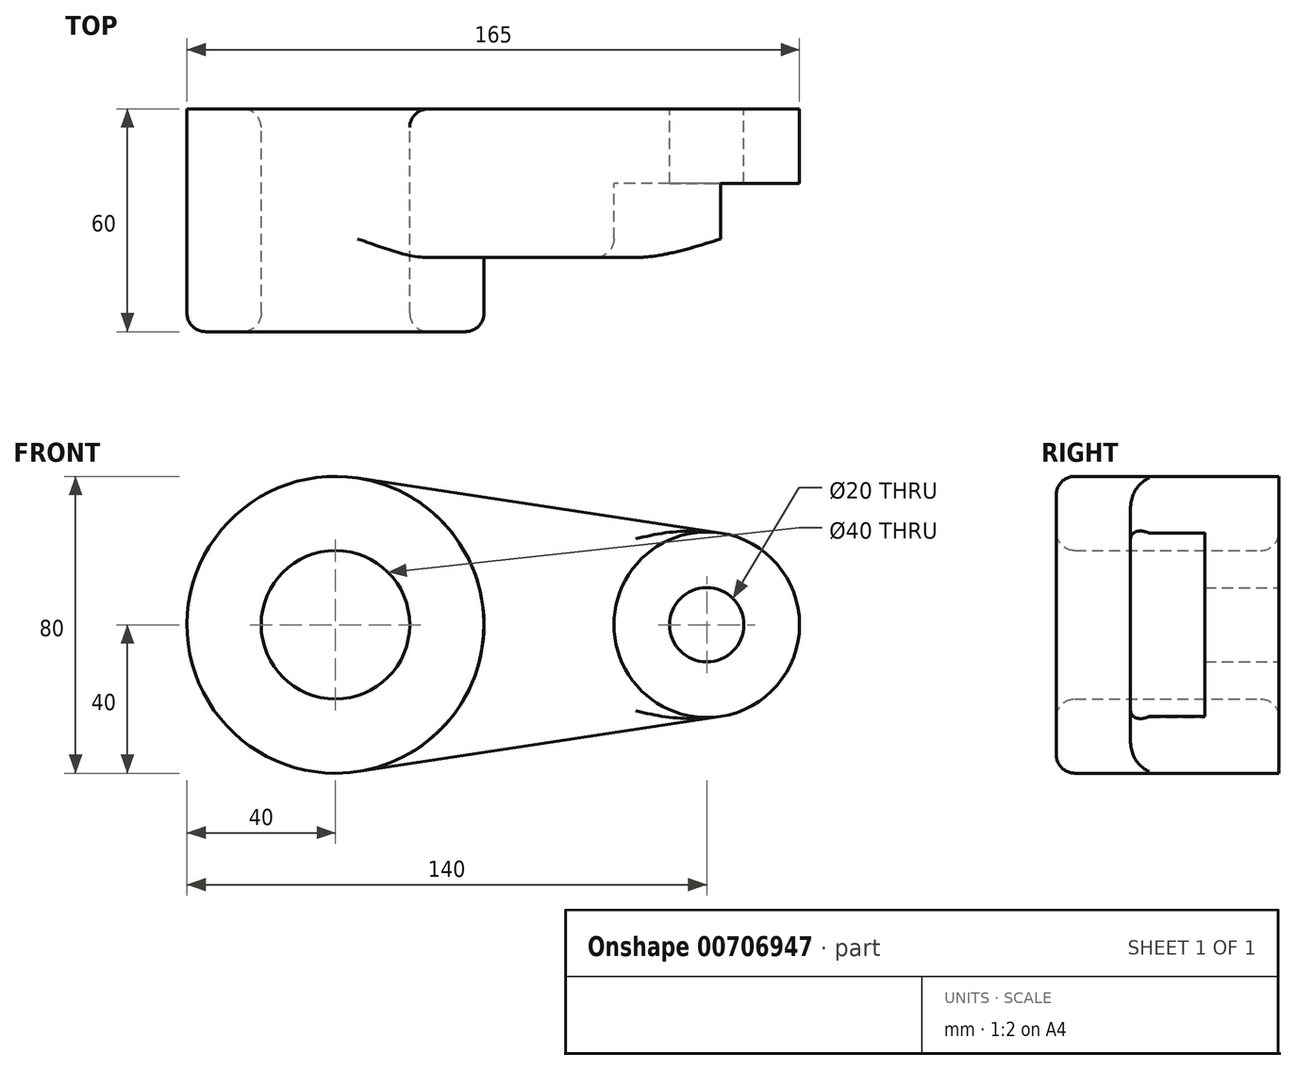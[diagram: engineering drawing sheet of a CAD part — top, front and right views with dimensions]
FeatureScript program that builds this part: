
annotation { "Feature Type Name" : "Feature", "Feature Type Description" : "" }
export const myFeature = defineFeature(function(context is Context, id is Id, definition is map)
    precondition{}
    {
        {
            var Q0;
            Q0=qCreatedBy(makeId("Front.planeOp"),FACE);
            var sketch = newSketch(context, id + "F0", { "sketchPlane" : qUnion([Q0])});
            skCircle(sketch, "E0", {"center": v(-50, 0) * mm, "radius": 40 * mm});
            skCircle(sketch, "E1", {"center": v(-50, 0) * mm, "radius": 20 * mm});
            skCircle(sketch, "E2", {"center": v(50, 0) * mm, "radius": 25 * mm});
            skCircle(sketch, "E3", {"center": v(50, 0) * mm, "radius": 10 * mm});
            skLineSegment(sketch, "E4", {"start": v(-44, 39.55) * mm, "end": v(53.75, 24.72) * mm});
            skLineSegment(sketch, "E5", {"start": v(-44, -39.55) * mm, "end": v(53.75, -24.72) * mm});
            skSolve(sketch);
        }
        {
            var Q0;
            Q0=makeQuery(id+"F0.imprint","IMPRINT",FACE,{"disambiguationData":[TD([[makeQuery(id+"F0.imprint","IMPRINT",EDGE,{"derivedFrom":sQuery(id+"F0.wireOp",EDGE,"E3")}),-1.0]])]});
            extrude(context, id + "F1", {"entities" : qUnion([Q0]), "depth" : 20 * mm, "offsetDistance" : 25 * mm});
        }
        {
            var Q0;
            {var subQ0=sQuery(id+"F0.wireOp",EDGE,"E4");Q0=makeQuery(id+"F0.imprint","IMPRINT",FACE,{"disambiguationData":[TD([[makeQuery(id+"F0.imprint","IMPRINT",EDGE,{"derivedFrom":subQ0}),-1.0]])]});}
            extrude(context, id + "F2", {"entities" : qUnion([Q0]), "operationType" : NewBodyOperationType.ADD, "depth" : 40 * mm, "offsetDistance" : 25 * mm});
        }
        {
            var Q0;
            Q0=makeQuery(id+"F0.imprint","IMPRINT",FACE,{"disambiguationData":[TD([[makeQuery(id+"F0.imprint","IMPRINT",EDGE,{"derivedFrom":sQuery(id+"F0.wireOp",EDGE,"E1")}),-1.0]])]});
            extrude(context, id + "F3", {"entities" : qUnion([Q0]), "operationType" : NewBodyOperationType.ADD, "depth" : 60 * mm, "offsetDistance" : 25 * mm});
        }
        {
            var Q0;
            Q0=makeQuery(id+"F3.opExtrude","CAP_EDGE",EDGE,{"disambiguationData":[OSD([sQuery(id+"F0.wireOp",EDGE,"E0")])],"isStart":false});
            var Q1;
            Q1=makeQuery(id+"F2.opExtrude","CAP_EDGE",EDGE,{"disambiguationData":[OSD([sQuery(id+"F0.wireOp",EDGE,"E4")])],"isStart":false});
            var Q2;
            Q2=makeQuery(id+"F2.opExtrude","CAP_EDGE",EDGE,{"disambiguationData":[OSD([sQuery(id+"F0.wireOp",EDGE,"E5")])],"isStart":false});
            var Q3;
            Q3=makeQuery(id+"F2.opExtrude","CAP_EDGE",EDGE,{"disambiguationData":[OSD([sQuery(id+"F0.wireOp",EDGE,"E2")])],"isStart":false});
            var Q4;
            Q4=makeQuery(id+"F3.opExtrude","SWEPT_FACE",FACE,{"disambiguationData":[OSD([sQuery(id+"F0.wireOp",EDGE,"E1")])]});
            var Q5;
            Q5=makeQuery(id+"F2.opExtrude","CAP_EDGE",EDGE,{"disambiguationData":[OSD([sQuery(id+"F0.wireOp",EDGE,"E0")])],"isStart":false});
            fillet(context, id + "F4", {"entities" : qUnion([Q0, Q1, Q2, Q3, Q4, Q5]), "radius" : 5 * mm, "tangentPropagation" : true, "allowEdgeOverflow" : false});
        }
    });
